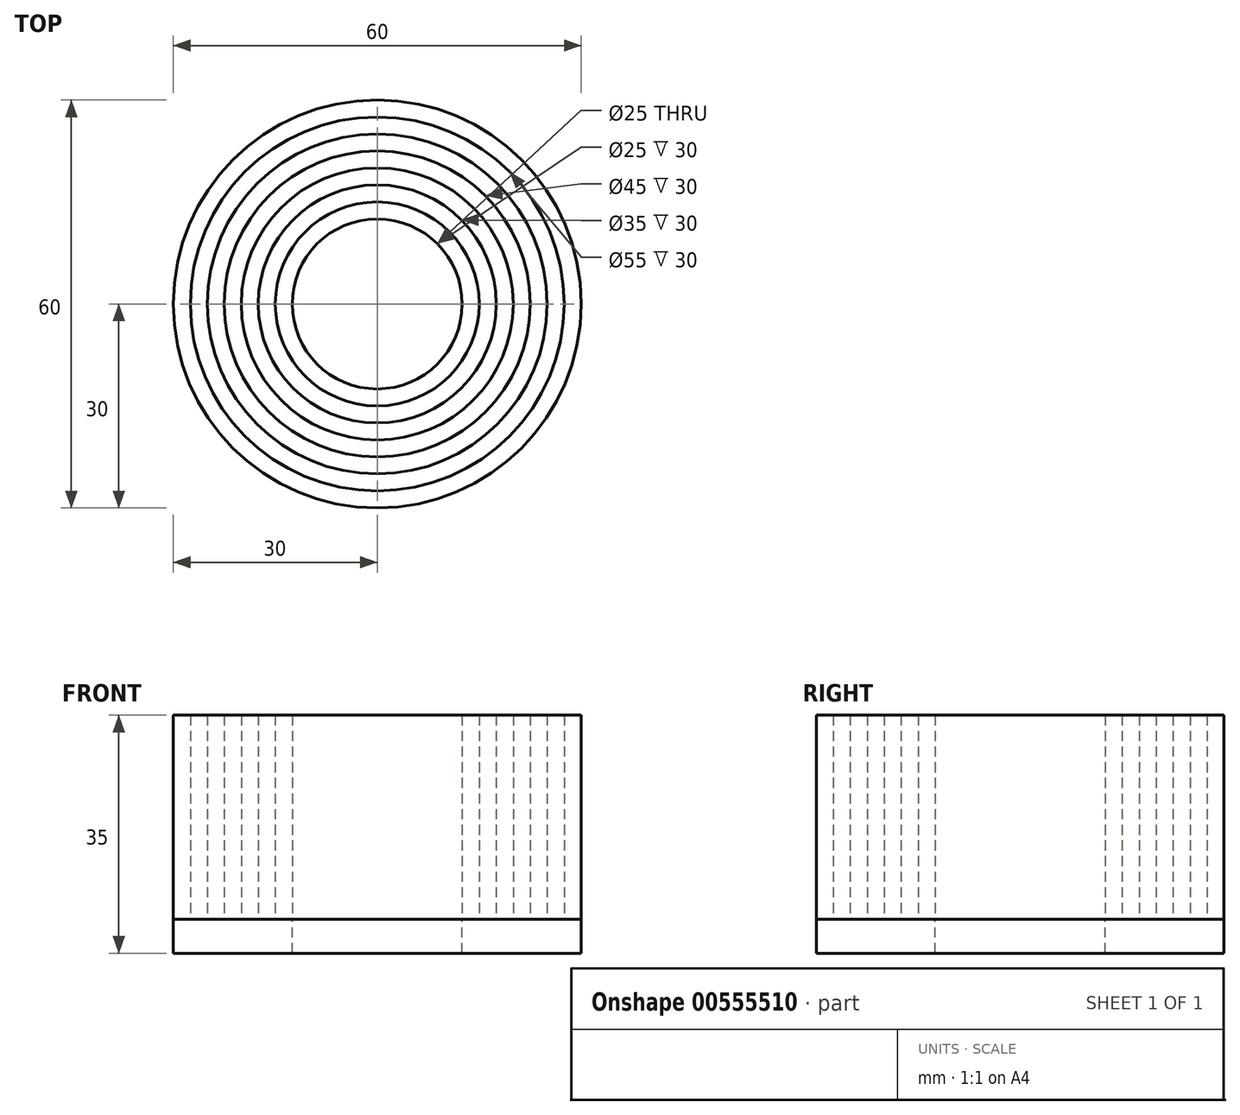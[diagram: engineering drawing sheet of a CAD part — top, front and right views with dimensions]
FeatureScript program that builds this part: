
annotation { "Feature Type Name" : "Feature", "Feature Type Description" : "" }
export const myFeature = defineFeature(function(context is Context, id is Id, definition is map)
    precondition{}
    {
        {
            var Q0;
            Q0=qCreatedBy(makeId("Top.planeOp"),FACE);
            var sketch = newSketch(context, id + "F0", { "sketchPlane" : qUnion([Q0])});
            skCircle(sketch, "E0", {"center": v(0, 0) * mm, "radius": 20 * mm});
            skCircle(sketch, "E1", {"center": v(0, 0) * mm, "radius": 22.5 * mm});
            skCircle(sketch, "E2", {"center": v(0, 0) * mm, "radius": 25 * mm});
            skCircle(sketch, "E3", {"center": v(0, 0) * mm, "radius": 27.5 * mm});
            skCircle(sketch, "E4", {"center": v(0, 0) * mm, "radius": 17.5 * mm});
            skCircle(sketch, "E5", {"center": v(0, 0) * mm, "radius": 30 * mm});
            skCircle(sketch, "E6", {"center": v(0, 0) * mm, "radius": 15 * mm});
            skCircle(sketch, "E7", {"center": v(0, 0) * mm, "radius": 12.5 * mm});
            skSolve(sketch);
        }
        {
            var Q0;
            Q0=makeQuery(id+"F0.imprint","IMPRINT",FACE,{"disambiguationData":[TD([[makeQuery(id+"F0.imprint","IMPRINT",EDGE,{"derivedFrom":sQuery(id+"F0.wireOp",EDGE,"E6")}),1.0]])]});
            var Q1;
            Q1=makeQuery(id+"F0.imprint","IMPRINT",FACE,{"disambiguationData":[TD([[makeQuery(id+"F0.imprint","IMPRINT",EDGE,{"derivedFrom":sQuery(id+"F0.wireOp",EDGE,"E0")}),1.0]])]});
            var Q2;
            Q2=makeQuery(id+"F0.imprint","IMPRINT",FACE,{"disambiguationData":[TD([[makeQuery(id+"F0.imprint","IMPRINT",EDGE,{"derivedFrom":sQuery(id+"F0.wireOp",EDGE,"E1")}),-1.0]])]});
            var Q3;
            Q3=makeQuery(id+"F0.imprint","IMPRINT",FACE,{"disambiguationData":[TD([[makeQuery(id+"F0.imprint","IMPRINT",EDGE,{"derivedFrom":sQuery(id+"F0.wireOp",EDGE,"E3")}),-1.0]])]});
            extrude(context, id + "F1", {"entities" : qUnion([Q0, Q1, Q2, Q3]), "depth" : 30 * mm, "offsetDistance" : 25 * mm});
        }
        {
            var Q0;
            Q0=qCreatedBy(makeId("Top.planeOp"),FACE);
            var sketch = newSketch(context, id + "F2", { "sketchPlane" : qUnion([Q0])});
            skCircle(sketch, "E8", {"center": v(0, 0) * mm, "radius": 30 * mm});
            skCircle(sketch, "E9", {"center": v(0, 0) * mm, "radius": 12.5 * mm});
            skSolve(sketch);
        }
        {
            var Q0;
            Q0 = qSketchRegion(id + "F2", true);
            extrude(context, id + "F3", {"entities" : qUnion([Q0]), "oppositeDirection" : true, "depth" : 5 * mm, "offsetDistance" : 25 * mm});
        }
    });
